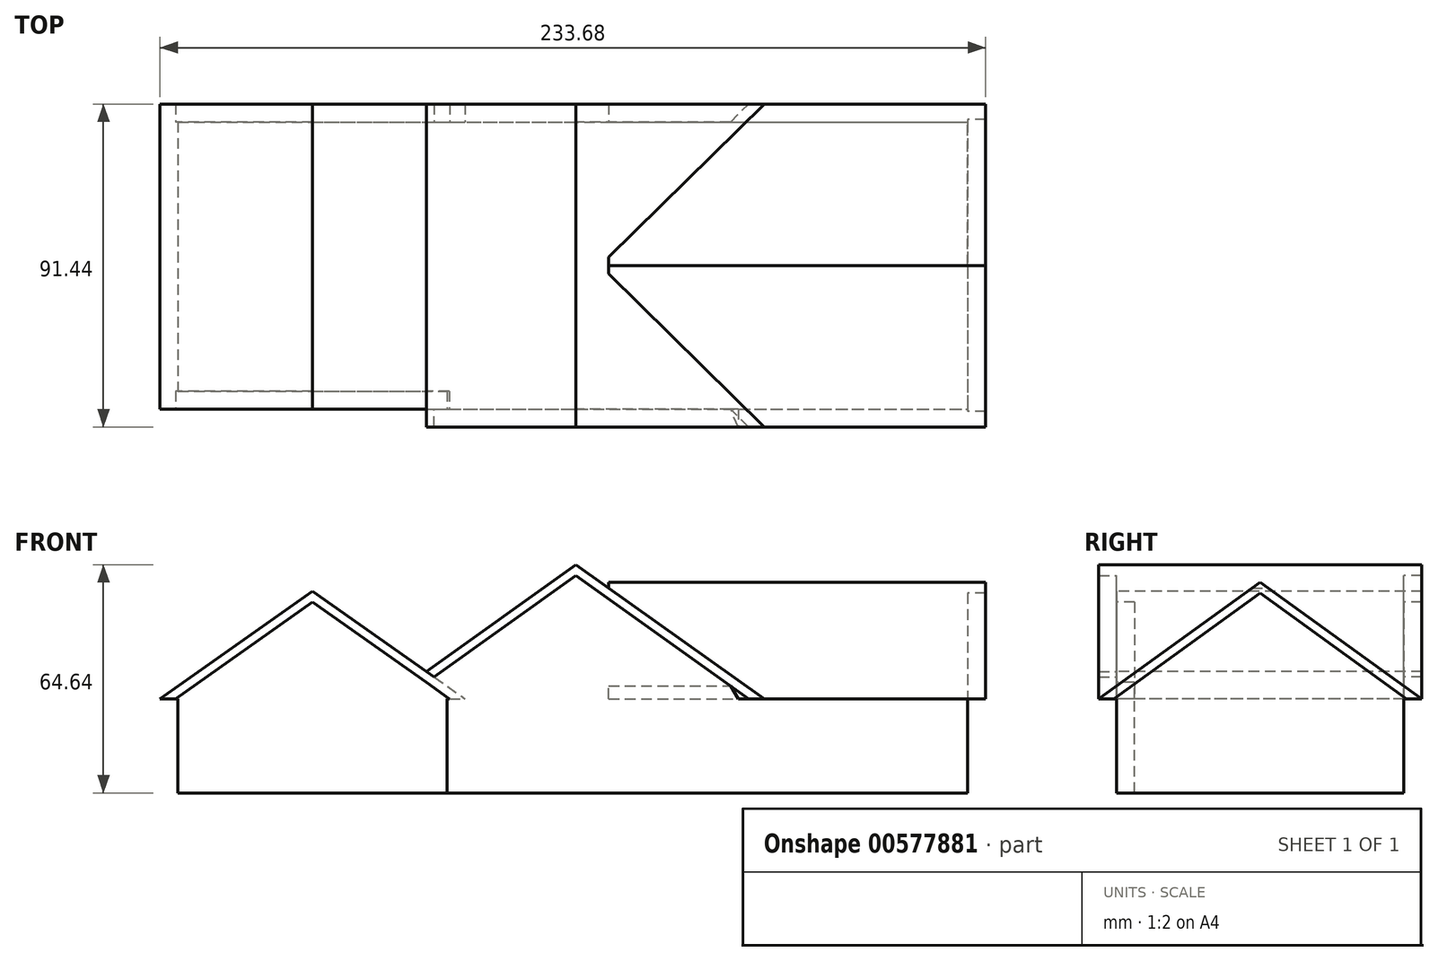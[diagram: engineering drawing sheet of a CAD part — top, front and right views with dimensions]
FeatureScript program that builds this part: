
annotation { "Feature Type Name" : "Feature", "Feature Type Description" : "" }
export const myFeature = defineFeature(function(context is Context, id is Id, definition is map)
    precondition{}
    {
        {
            var Q0;
            Q0=qCreatedBy(makeId("Front.planeOp"),FACE);
            var sketch = newSketch(context, id + "F0", { "sketchPlane" : qUnion([Q0])});
            skLineSegment(sketch, "E0.bottom", {"start": v(-33.08, 11.33) * mm, "end": v(78.68, 11.33) * mm});
            skLineSegment(sketch, "E0.top", {"start": v(-33.08, -15.34) * mm, "end": v(78.68, -15.34) * mm});
            skLineSegment(sketch, "E0.left", {"start": v(-33.08, 11.33) * mm, "end": v(-33.08, -15.34) * mm});
            skLineSegment(sketch, "E0.right", {"start": v(78.68, 11.33) * mm, "end": v(78.68, -15.34) * mm});
            skSolve(sketch);
        }
        {
            var Q0;
            Q0=makeQuery(id+"F0.imprint","IMPRINT",FACE,{"disambiguationData":[TD([[makeQuery(id+"F0.imprint","IMPRINT",EDGE,{"derivedFrom":sQuery(id+"F0.wireOp",EDGE,"E0.bottom")}),-1.0]])]});
            extrude(context, id + "F1", {"entities" : qUnion([Q0]), "oppositeDirection" : true, "depth" : 81.28 * mm, "offsetDistance" : 25.4 * mm});
        }
        {
            var Q0;
            Q0=makeQuery(id+"F1.opExtrude","SWEPT_FACE",FACE,{"disambiguationData":[OSD([sQuery(id+"F0.wireOp",EDGE,"E0.left")])]});
            var sketch = newSketch(context, id + "F2", { "sketchPlane" : qUnion([Q0])});
            skLineSegment(sketch, "E1", {"start": v(-81.28, 11.33) * mm, "end": v(-81.28, -15.34) * mm});
            skLineSegment(sketch, "E2", {"start": v(-81.28, -15.34) * mm, "end": v(0, -15.34) * mm});
            skLineSegment(sketch, "E3", {"start": v(0, -15.34) * mm, "end": v(0, 11.33) * mm});
            skLineSegment(sketch, "E4", {"start": v(0, 11.33) * mm, "end": v(-81.28, 11.33) * mm});
            skSolve(sketch);
        }
        {
            var Q0;
            Q0=makeQuery(id+"F2.imprint","IMPRINT",FACE,{"disambiguationData":[TD([[makeQuery(id+"F2.imprint","IMPRINT",EDGE,{"derivedFrom":sQuery(id+"F2.wireOp",EDGE,"E1")}),1.0]])]});
            extrude(context, id + "F3", {"entities" : qUnion([Q0]), "operationType" : NewBodyOperationType.ADD, "depth" : 35.56 * mm, "offsetDistance" : 25.4 * mm});
        }
        {
            var Q0;
            Q0=makeQuery(id+"F3.opExtrude","CAP_FACE",FACE,{"disambiguationData":[OSD([sQuery(id+"F2.wireOp",EDGE,"E1"),sQuery(id+"F2.wireOp",EDGE,"E2"),sQuery(id+"F2.wireOp",EDGE,"E3"),sQuery(id+"F2.wireOp",EDGE,"E4")])],"isStart":false});
            var sketch = newSketch(context, id + "F4", { "sketchPlane" : qUnion([Q0])});
            skLineSegment(sketch, "E5", {"start": v(-81.28, 11.33) * mm, "end": v(-81.28, -15.34) * mm});
            skLineSegment(sketch, "E6", {"start": v(-81.28, -15.34) * mm, "end": v(-5.08, -15.34) * mm});
            skLineSegment(sketch, "E7", {"start": v(-5.08, -15.34) * mm, "end": v(-5.08, 11.33) * mm});
            skLineSegment(sketch, "E8", {"start": v(-5.08, 11.33) * mm, "end": v(-81.28, 11.33) * mm});
            skSolve(sketch);
        }
        {
            var Q0;
            {var subQ0=sQuery(id+"F4.wireOp",EDGE,"E5");Q0=makeQuery(id+"F4.imprint","IMPRINT",FACE,{"disambiguationData":[TD([[makeQuery(id+"F4.imprint","IMPRINT",EDGE,{"derivedFrom":subQ0}),1.0]])]});}
            var Q1;
            {var subQ2=sQuery(id+"F4.wireOp",EDGE,"E7");Q1=makeQuery(id+"F4.imprint","IMPRINT",FACE,{"disambiguationData":[TD([[makeQuery(id+"F4.imprint","IMPRINT",EDGE,{"derivedFrom":subQ2}),1.0]])]});}
            extrude(context, id + "F5", {"entities" : qUnion([Q0, Q1]), "operationType" : NewBodyOperationType.ADD, "depth" : 76.2 * mm, "offsetDistance" : 25.4 * mm});
        }
        {
            var Q0;
            Q0=makeQuery(id+"F5.opExtrude","SWEPT_FACE",FACE,{"disambiguationData":[OSD([sQuery(id+"F4.wireOp",EDGE,"E7")])]});
            var sketch = newSketch(context, id + "F6", { "sketchPlane" : qUnion([Q0])});
            skLineSegment(sketch, "E9", {"start": v(-144.84, 11.33) * mm, "end": v(-149.92, 11.33) * mm});
            skLineSegment(sketch, "E10", {"start": v(-68.64, 11.33) * mm, "end": v(-63.56, 11.33) * mm});
            skPoint(sketch, "E11", {"position": v(-106.74, 41.8) * mm});
            skPoint(sketch, "E11.positionSnap0", {"position": v(-106.74, 11.33) * mm});
            skLineSegment(sketch, "E12", {"start": v(-106.74, 41.8) * mm, "end": v(-149.92, 11.33) * mm});
            skLineSegment(sketch, "E13", {"start": v(-106.74, 41.8) * mm, "end": v(-63.56, 11.33) * mm});
            skLineSegment(sketch, "E14.0", {"start": v(-106.74, 38.7) * mm, "end": v(-67.96, 11.33) * mm});
            skLineSegment(sketch, "E14.1", {"start": v(-106.74, 38.7) * mm, "end": v(-145.52, 11.33) * mm});
            skSolve(sketch);
        }
        {
            var Q0;
            {var subQ0=sQuery(id+"F6.wireOp",EDGE,"E14.0");Q0=makeQuery(id+"F6.imprint","IMPRINT",FACE,{"disambiguationData":[TD([[makeQuery(id+"F6.imprint","IMPRINT",EDGE,{"derivedFrom":subQ0}),-1.0]])]});}
            extrude(context, id + "F7", {"entities" : qUnion([Q0]), "operationType" : NewBodyOperationType.ADD, "oppositeDirection" : true, "depth" : 76.2 * mm, "offsetDistance" : 25.4 * mm});
        }
        {
            var Q0;
            {var subQ1=sQuery(id+"F6.wireOp",EDGE,"E12");Q0=makeQuery(id+"F6.imprint","IMPRINT",FACE,{"disambiguationData":[TD([[makeQuery(id+"F6.imprint","IMPRINT",EDGE,{"derivedFrom":subQ1}),1.0]])]});}
            extrude(context, id + "F8", {"entities" : qUnion([Q0]), "oppositeDirection" : true, "depth" : 81.28 * mm, "offsetDistance" : 25.4 * mm});
        }
        {
            var Q0;
            Q0=makeQuery(id+"F8.opExtrude","CAP_FACE",FACE,{"disambiguationData":[OSD([sQuery(id+"F6.wireOp",EDGE,"E9"),sQuery(id+"F6.wireOp",EDGE,"E10"),sQuery(id+"F6.wireOp",EDGE,"E12"),sQuery(id+"F6.wireOp",EDGE,"E13"),sQuery(id+"F6.wireOp",EDGE,"E14.0"),sQuery(id+"F6.wireOp",EDGE,"E14.1")])],"isStart":true});
            extrude(context, id + "F9", {"entities" : qUnion([Q0]), "operationType" : NewBodyOperationType.ADD, "depth" : 5.08 * mm, "offsetDistance" : 25.4 * mm});
        }
        {
            var Q0;
            Q0=makeQuery(id+"F1.opExtrude","CAP_FACE",FACE,{"disambiguationData":[OSD([sQuery(id+"F0.wireOp",EDGE,"E0.bottom"),sQuery(id+"F0.wireOp",EDGE,"E0.top"),sQuery(id+"F0.wireOp",EDGE,"E0.left"),sQuery(id+"F0.wireOp",EDGE,"E0.right")])],"isStart":true});
            var sketch = newSketch(context, id + "F10", { "sketchPlane" : qUnion([Q0])});
            skLineSegment(sketch, "E15", {"start": v(-85.6, 11.08) * mm, "end": v(21.08, 11.33) * mm});
            skPoint(sketch, "E16", {"position": v(-32.26, 49.3) * mm});
            skPoint(sketch, "E16.positionSnap0", {"position": v(-32.26, 11.2) * mm});
            skLineSegment(sketch, "E17", {"start": v(-85.6, 11.08) * mm, "end": v(-32.26, 49.3) * mm});
            skLineSegment(sketch, "E18", {"start": v(21.08, 11.33) * mm, "end": v(-32.26, 49.3) * mm});
            skLineSegment(sketch, "E19.0", {"start": v(16.71, 11.32) * mm, "end": v(-32.26, 46.18) * mm});
            skLineSegment(sketch, "E19.1", {"start": v(-81.23, 11.1) * mm, "end": v(-32.26, 46.18) * mm});
            skLineSegment(sketch, "E20", {"start": v(-76.67, 17.48) * mm, "end": v(-74.5, 15.91) * mm});
            skLineSegment(sketch, "E21", {"start": v(-74.5, 15.91) * mm, "end": v(-67.71, 11.12) * mm});
            skSolve(sketch);
        }
        {
            var Q0;
            {var subQ0=sQuery(id+"F10.wireOp",EDGE,"E19.1");Q0=makeQuery(id+"F10.imprint","IMPRINT",FACE,{"disambiguationData":[TD([[makeQuery(id+"F10.imprint","IMPRINT",EDGE,{"derivedFrom":subQ0}),-1.0]])]});}
            extrude(context, id + "F11", {"entities" : qUnion([Q0]), "operationType" : NewBodyOperationType.ADD, "oppositeDirection" : true, "depth" : 81.28 * mm, "offsetDistance" : 25.4 * mm});
        }
        {
            var Q0;
            {var subQ5=sQuery(id+"F10.wireOp",EDGE,"E18");Q0=makeQuery(id+"F10.imprint","IMPRINT",FACE,{"disambiguationData":[TD([[makeQuery(id+"F10.imprint","IMPRINT",EDGE,{"derivedFrom":subQ5}),1.0]])]});}
            extrude(context, id + "F12", {"entities" : qUnion([Q0]), "operationType" : NewBodyOperationType.ADD, "oppositeDirection" : true, "depth" : 86.36 * mm, "offsetDistance" : 25.4 * mm});
        }
        {
            var Q0;
            {var subQ5=sQuery(id+"F10.wireOp",EDGE,"E18");Q0=makeQuery(id+"F10.imprint","IMPRINT",FACE,{"disambiguationData":[TD([[makeQuery(id+"F10.imprint","IMPRINT",EDGE,{"derivedFrom":subQ5}),1.0]])]});}
            extrude(context, id + "F13", {"entities" : qUnion([Q0]), "operationType" : NewBodyOperationType.ADD, "depth" : 5.08 * mm, "offsetDistance" : 25.4 * mm});
        }
        {
            var Q0;
            Q0=makeQuery(id+"F1.opExtrude","SWEPT_FACE",FACE,{"disambiguationData":[OSD([sQuery(id+"F0.wireOp",EDGE,"E0.right")])]});
            var sketch = newSketch(context, id + "F14", { "sketchPlane" : qUnion([Q0])});
            skLineSegment(sketch, "E22", {"start": v(0, 11.33) * mm, "end": v(-5.08, 11.33) * mm});
            skLineSegment(sketch, "E23", {"start": v(81.28, 11.33) * mm, "end": v(86.36, 11.33) * mm});
            skPoint(sketch, "E24", {"position": v(40.64, 44.35) * mm});
            skPoint(sketch, "E24.positionSnap0", {"position": v(40.64, 11.33) * mm});
            skLineSegment(sketch, "E25", {"start": v(40.64, 44.35) * mm, "end": v(-5.08, 11.33) * mm});
            skLineSegment(sketch, "E26", {"start": v(40.64, 44.35) * mm, "end": v(86.36, 11.33) * mm});
            skLineSegment(sketch, "E27.0", {"start": v(40.64, 41.22) * mm, "end": v(-0.74, 11.33) * mm});
            skLineSegment(sketch, "E27.1", {"start": v(40.64, 41.22) * mm, "end": v(82.02, 11.33) * mm});
            skSolve(sketch);
        }
        {
            var Q0;
            {var subQ0=sQuery(id+"F14.wireOp",EDGE,"E27.0");Q0=makeQuery(id+"F14.imprint","IMPRINT",FACE,{"disambiguationData":[TD([[makeQuery(id+"F14.imprint","IMPRINT",EDGE,{"derivedFrom":subQ0}),1.0]])]});}
            extrude(context, id + "F15", {"entities" : qUnion([Q0]), "operationType" : NewBodyOperationType.ADD, "oppositeDirection" : true, "depth" : 101.6 * mm, "offsetDistance" : 25.4 * mm});
        }
        {
            var Q0;
            {var subQ1=sQuery(id+"F14.wireOp",EDGE,"E25");Q0=makeQuery(id+"F14.imprint","IMPRINT",FACE,{"disambiguationData":[TD([[makeQuery(id+"F14.imprint","IMPRINT",EDGE,{"derivedFrom":subQ1}),1.0]])]});}
            extrude(context, id + "F16", {"entities" : qUnion([Q0]), "operationType" : NewBodyOperationType.ADD, "oppositeDirection" : true, "depth" : 101.6 * mm, "offsetDistance" : 25.4 * mm});
        }
        {
            var Q0;
            {var subQ1=sQuery(id+"F14.wireOp",EDGE,"E25");Q0=makeQuery(id+"F14.imprint","IMPRINT",FACE,{"disambiguationData":[TD([[makeQuery(id+"F14.imprint","IMPRINT",EDGE,{"derivedFrom":subQ1}),1.0]])]});}
            extrude(context, id + "F17", {"entities" : qUnion([Q0]), "operationType" : NewBodyOperationType.ADD, "depth" : 5.08 * mm, "offsetDistance" : 25.4 * mm});
        }
        {
            var Q0;
            Q0=makeQuery(id+"F13.opExtrude","CAP_FACE",FACE,{"disambiguationData":[OSD([sQuery(id+"F10.wireOp",EDGE,"E15"),sQuery(id+"F10.wireOp",EDGE,"E17"),sQuery(id+"F10.wireOp",EDGE,"E18"),sQuery(id+"F10.wireOp",EDGE,"E19.0"),sQuery(id+"F10.wireOp",EDGE,"E19.1")])],"isStart":false});
            var sketch = newSketch(context, id + "F18", { "sketchPlane" : qUnion([Q0])});
            skLineSegment(sketch, "E28", {"start": v(-22.92, 15) * mm, "end": v(-22.92, 11.33) * mm});
            skLineSegment(sketch, "E29", {"start": v(-22.92, 11.33) * mm, "end": v(13.73, 11.33) * mm});
            skLineSegment(sketch, "E30", {"start": v(13.73, 11.33) * mm, "end": v(11.55, 15) * mm});
            skLineSegment(sketch, "E31", {"start": v(11.55, 15) * mm, "end": v(-22.92, 15) * mm});
            skSolve(sketch);
        }
        {
            var Q0;
            Q0=makeQuery(id+"F18.imprint","IMPRINT",FACE,{"disambiguationData":[TD([[makeQuery(id+"F18.imprint","IMPRINT",EDGE,{"derivedFrom":sQuery(id+"F18.wireOp",EDGE,"E28")}),1.0]])]});
            extrude(context, id + "F19", {"entities" : qUnion([Q0]), "operationType" : NewBodyOperationType.REMOVE, "oppositeDirection" : true, "depth" : 5.08 * mm, "offsetDistance" : 25.4 * mm});
        }
    });
